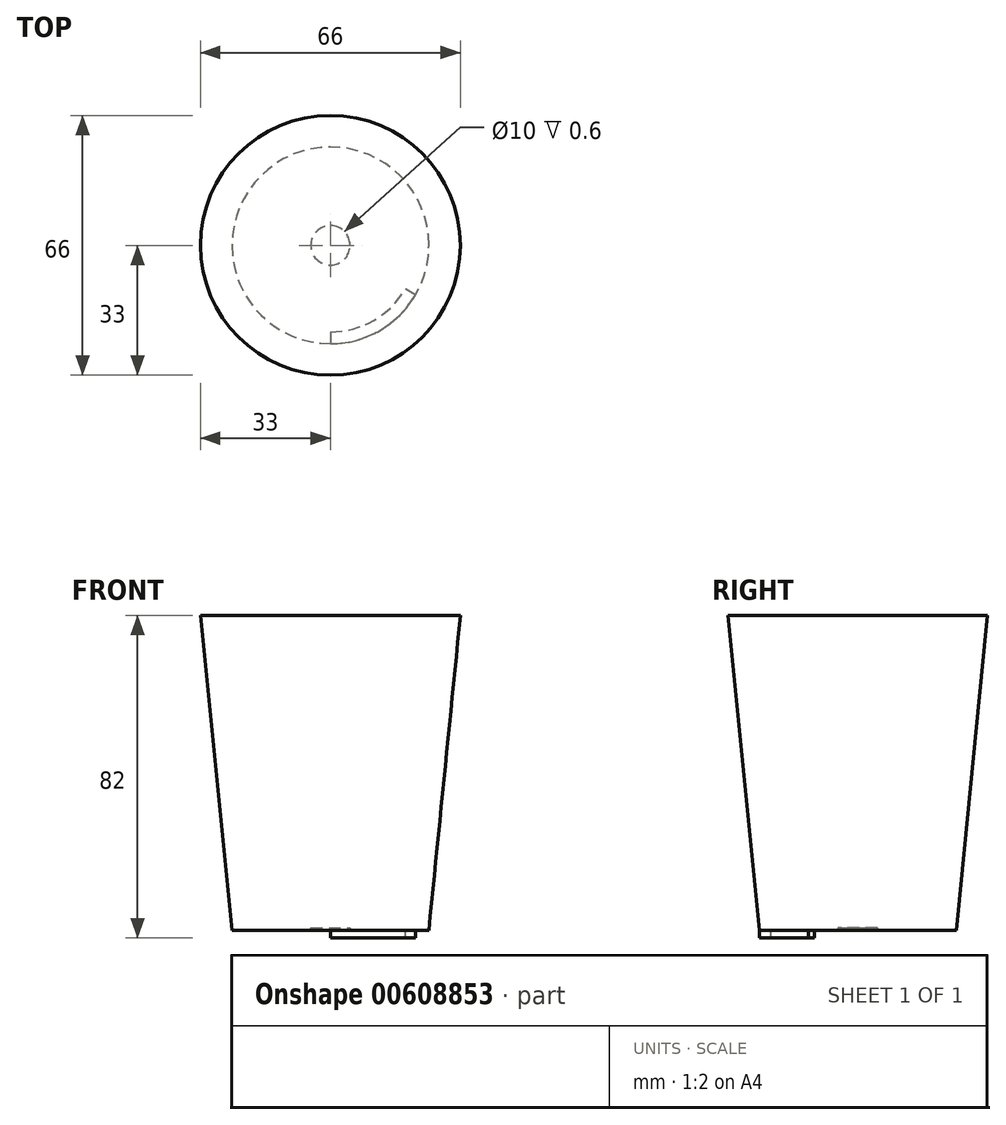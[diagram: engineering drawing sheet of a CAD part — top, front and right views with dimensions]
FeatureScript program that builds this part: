
annotation { "Feature Type Name" : "Feature", "Feature Type Description" : "" }
export const myFeature = defineFeature(function(context is Context, id is Id, definition is map)
    precondition{}
    {
        {
            assignVariable(context, id + "F0", {"name" : "h", "anyValue" : 80 * mm});
        }
        {
            var Q0;
            Q0=qCreatedBy(makeId("Top.planeOp"),FACE);
            cPlane(context, id + "F1", {"entities" : qUnion([Q0]), "cplaneType" : CPlaneType.OFFSET, "offset" : getVariable(context, 'h'), "width" : 150 * mm, "height" : 150 * mm});
        }
        {
            var Q0;
            Q0=qCreatedBy(makeId("Top.planeOp"),FACE);
            var sketch = newSketch(context, id + "F2", { "sketchPlane" : qUnion([Q0])});
            skCircle(sketch, "E0", {"center": v(0, 0) * mm, "radius": 25 * mm});
            skSolve(sketch);
        }
        {
            var Q0;
            Q0=qCreatedBy(id+"F1.planeOp",FACE);
            var sketch = newSketch(context, id + "F3", { "sketchPlane" : qUnion([Q0])});
            skCircle(sketch, "E1", {"center": v(0, 0) * mm, "radius": 33 * mm});
            skSolve(sketch);
        }
        {
            var Q0;
            Q0=makeQuery(id+"F2.imprint","IMPRINT",FACE,{"disambiguationData":[TD([[makeQuery(id+"F2.imprint","IMPRINT",EDGE,{"derivedFrom":sQuery(id+"F2.wireOp",EDGE,"E0")}),1.0]])]});
            var Q1;
            Q1=makeQuery(id+"F3.imprint","IMPRINT",FACE,{"disambiguationData":[TD([[makeQuery(id+"F3.imprint","IMPRINT",EDGE,{"derivedFrom":sQuery(id+"F3.wireOp",EDGE,"E1")}),1.0]])]});
            loft(context, id + "F4", {"sheetProfilesArray" : [{ "sheetProfileEntities" : qUnion([Q0]) }, { "sheetProfileEntities" : qUnion([Q1]) }]});
        }
        {
            var Q0;
            Q0=makeQuery(id+"F4.opLoft","CAP_FACE",FACE,{"disambiguationData":[OSD([makeQuery(id+"F2.imprint","IMPRINT",FACE,{"disambiguationData":[TD([[makeQuery(id+"F2.imprint","IMPRINT",EDGE,{"derivedFrom":sQuery(id+"F2.wireOp",EDGE,"E0")}),1.0]])]})])],"isStart":true});
            var sketch = newSketch(context, id + "F5", { "sketchPlane" : qUnion([Q0])});
            skCircle(sketch, "E2", {"center": v(0, 0) * mm, "radius": 5 * mm});
            skSolve(sketch);
        }
        {
            var Q0;
            Q0=makeQuery(id+"F5.imprint","IMPRINT",FACE,{"disambiguationData":[TD([[makeQuery(id+"F5.imprint","IMPRINT",EDGE,{"derivedFrom":sQuery(id+"F5.wireOp",EDGE,"E2")}),1.0]])]});
            extrude(context, id + "F6", {"entities" : qUnion([Q0]), "operationType" : NewBodyOperationType.REMOVE, "oppositeDirection" : true, "depth" : 0.6 * mm, "offsetDistance" : 25 * mm});
        }
        {
            var Q0;
            Q0=makeQuery(id+"F4.opLoft","CAP_FACE",FACE,{"disambiguationData":[OSD([makeQuery(id+"F2.imprint","IMPRINT",FACE,{"disambiguationData":[TD([[makeQuery(id+"F2.imprint","IMPRINT",EDGE,{"derivedFrom":sQuery(id+"F2.wireOp",EDGE,"E0")}),1.0]])]})])],"isStart":true});
            var sketch = newSketch(context, id + "F7", { "sketchPlane" : qUnion([Q0])});
            skArc(sketch, "E3", {"start": v(0, 25) * mm, "mid": v(12.5, 21.65) * mm, "end": v(21.65, 12.5) * mm});
            skLineSegment(sketch, "E4", {"start": v(0, 0) * mm, "end": v(0, 25) * mm, "construction": true});
            skLineSegment(sketch, "E5", {"start": v(0, 0) * mm, "end": v(21.65, 12.5) * mm, "construction": true});
            skArc(sketch, "E6", {"start": v(0, 22) * mm, "mid": v(11, 19.05) * mm, "end": v(19.05, 11) * mm});
            skLineSegment(sketch, "E7", {"start": v(0, 22) * mm, "end": v(0, 25) * mm});
            skLineSegment(sketch, "E8", {"start": v(19.05, 11) * mm, "end": v(21.65, 12.5) * mm});
            skSolve(sketch);
        }
        {
            var Q0;
            Q0=makeQuery(id+"F7.imprint","IMPRINT",FACE,{"disambiguationData":[TD([[makeQuery(id+"F7.imprint","IMPRINT",EDGE,{"derivedFrom":sQuery(id+"F7.wireOp",EDGE,"19992b06-d49f-487a-8428-ab4264d28d9c.1.0")}),1.0]])]});
            var Q1;
            Q1=makeQuery(id+"F7.imprint","IMPRINT",FACE,{"disambiguationData":[TD([[makeQuery(id+"F7.imprint","IMPRINT",EDGE,{"derivedFrom":sQuery(id+"F7.wireOp",EDGE,"E3")}),-1.0]])]});
            var Q2;
            Q2=makeQuery(id+"F7.imprint","IMPRINT",FACE,{"disambiguationData":[TD([[makeQuery(id+"F7.imprint","IMPRINT",EDGE,{"derivedFrom":sQuery(id+"F7.wireOp",EDGE,"19992b06-d49f-487a-8428-ab4264d28d9c.2.0")}),1.0]])]});
            extrude(context, id + "F8", {"entities" : qUnion([Q0, Q1, Q2]), "depth" : 2 * mm, "offsetDistance" : 25 * mm});
        }
    });
